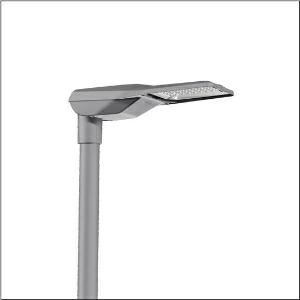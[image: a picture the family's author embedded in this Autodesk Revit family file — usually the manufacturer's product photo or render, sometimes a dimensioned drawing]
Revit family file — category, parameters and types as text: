
# Revit family: streetlight_sl_21_iq_mini___stw1_0a_5xe2e41d08hb_667c
name_source: partatom
category: Lighting Fixtures
units: mm (PartAtom-declared; Revit-internal decimal feet)

## family parameters
Cut with Voids When Loaded = No
Host = Face
Light Source = No
Part Type = Normal
Room Calculation Point = No
Round Connector Dimension = Use Diameter
Shared = No

## types (1)
- --- (1 x LED, 9860 lm, 70.9 W, 4000K)
    Apparent Load = 71 VA
    CIE Flux Codes = 38 75 98 100 100
    Color Rendering = 70
    Color Temperature = 4000K
    Default Elevation = 1800 mm
    Description = Streetlight SL 21 iQ mini, mast luminaire, primary light control with lens, of PMMA, primary optical cover: cover, of toughened safety glass, transparent, light distribution: STW1.0a, light emission: direct distribution, primary light characteristic: asymmetric, installation type: post-top, side-entry, LED, High Power LED, rated luminous flux: 9.860lm, luminous efficacy: 139lm/W, light colour: 740, colour temperature: 4000K, control: Auto-Match, Temp-Guard, Lumen-Switch, Night-Set, Smart-Wire, Light-Fading, Desk-Remote (wireless, voltage-free reading and setting of iQ features in the workshop via application-optimized NFC function/RFID function), optimised constant luminous flux control (CLO 2.0), presetting dimming linear, mains connection: 220..240V, AC, 50/60Hz, start of lifetime: 71W, end of service life: 75W, reduction: 31W, luminaire housing, of diecast aluminium, powder-coated, Siteco® metallic grey (DB 702S), corrosivity category C5 mid according to DIN EN ISO 12944, please order mast flange separately, inclination adjustable: 0°, 5°, 10°, 15°, sealing non-destructively replaceable, multi-level sealing system, length: 628mm, width: 235mm, height: 110mm, mast flange for spigot size: 42mm (side-entry): 5XC10008XM4, 60/48mm (side-entry/post-top): 5XC10108XM2, 76/60mm (side-entry/post-top): 5XC10108XM1, protection rating (complete): IP66, insulation class (complete): insulation class II (safety insulation), certification: CE, ENEC, ENEC+, VDE, impact resistance: IK09, permissible operating ambient temperature for outdoor applications: -40..+50°C, standard-compliant lighting for roads and squares, packaging unit: 1 piece

Light Distribution: STW1.0a
    Height = 110 mm
    Lamp = 1 x LED
    Lamp Light Flux = 9860 lm
    Lamp Power = 70.9 W
    Lamp count = 1
    Length = 625 mm
    Luminous efficacy = 139 lm/W
    Manufacturer = Siteco
    ModVariant = No
    Model = 5XE2E41D08HB
    Number of Poles = 1
    OnlyDefault = Yes
    Power Factor = 1
    Product Name = Streetlight SL 21 iQ mini | STW1.0a
    Product group = mast luminaire | pylon top
    ProductGroupID = 6100
    Protection Class = Protection class II
    Protection Degree = IP 66
    RLX_Detail_Level = 1
    RLX_Emergency_Light_Flux = 0 lm
    RLX_Emergency_Type = 0
    RLX_Emergency_Type_DB = No
    RlxData = <blob elided: 92181 chars, md5=9451f430>
    Socket = socket
    Standby Power = 0 W
    System Light Flux = 9860 lm
    System Power = 71 W
    Type Comments = factory setting: luminous flux: 100 % | dim-lin: 254 | 711 mA
    Type Image = l_1003519.jpg
    URL = http://relux.com
    VarID = @adj_107967
    Voltage = 0 V
    Weight = 0.00 kg
    Width = 234 mm

## geometry (parser evidence)
native form markers: Blend x4, Sweep x11
no freeform markers — native parametric forms only
